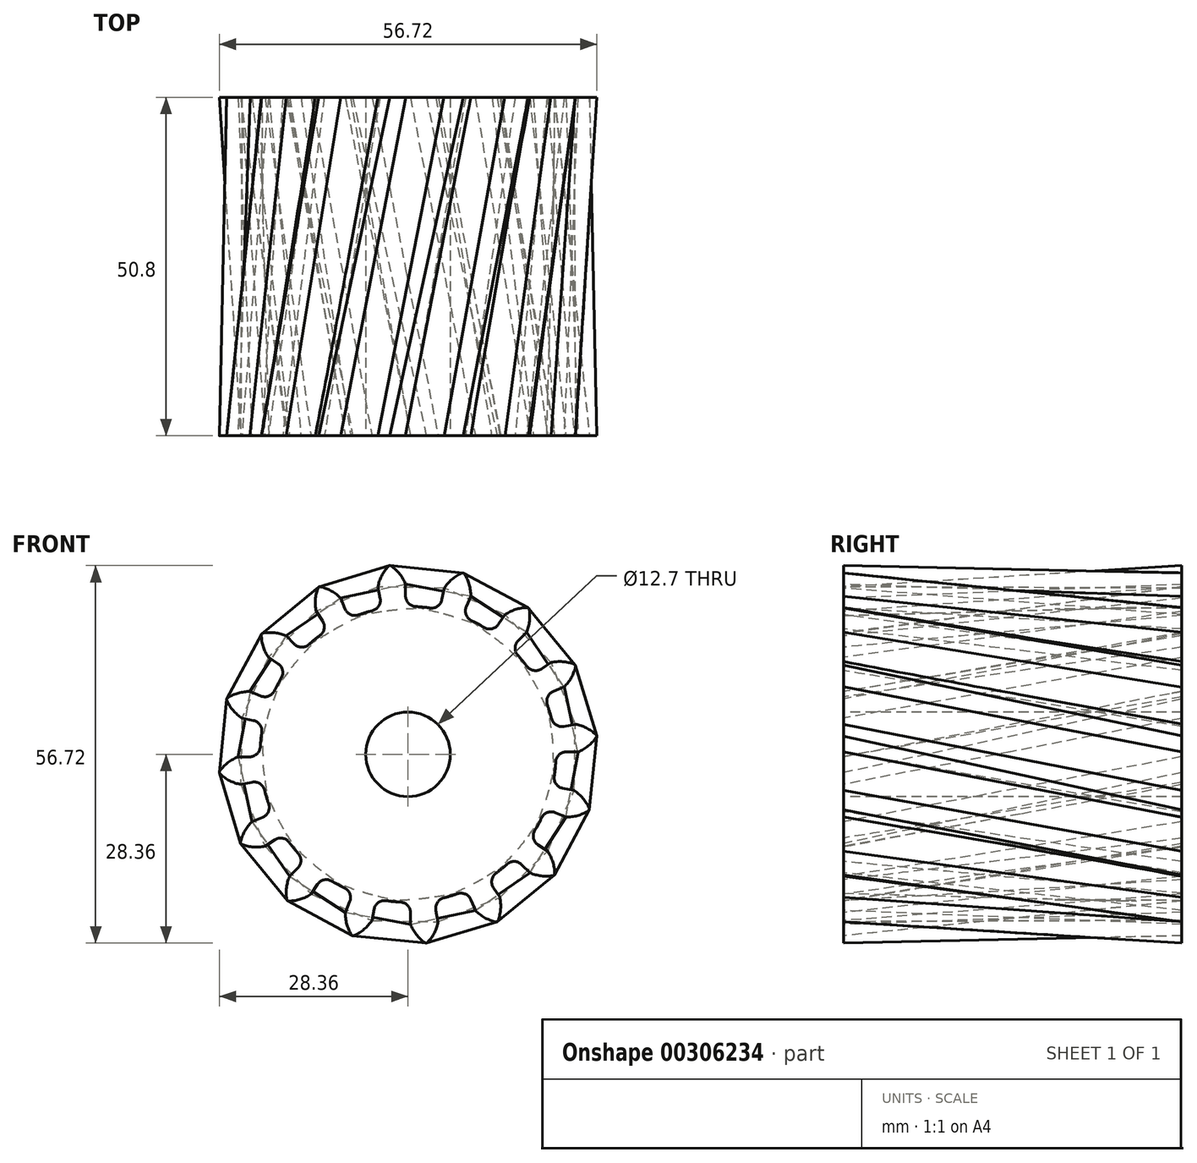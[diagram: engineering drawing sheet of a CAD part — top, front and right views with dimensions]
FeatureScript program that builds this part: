
annotation { "Feature Type Name" : "Feature", "Feature Type Description" : "" }
export const myFeature = defineFeature(function(context is Context, id is Id, definition is map)
    precondition{}
    {
        {
            var Q0;
            Q0=qCreatedBy(makeId("Front.planeOp"),FACE);
            var sketch = newSketch(context, id + "F0", { "sketchPlane" : qUnion([Q0])});
            skArc(sketch, "E0", {"start": v(-5.4, 21.56) * mm, "mid": v(-6.42, 21.28) * mm, "end": v(-7.42, 20.95) * mm});
            skLineSegment(sketch, "E1", {"start": v(0, 0) * mm, "end": v(-4.33, 44.68) * mm, "construction": true});
            skLineSegment(sketch, "E2", {"start": v(-2.75, 28.36) * mm, "end": v(-2.8, 28.36) * mm});
            skLineSegment(sketch, "E3", {"start": v(-0.36, 25.53) * mm, "end": v(-0.36, 23.8) * mm});
            skArc(sketch, "E4.trimOffspring", {"start": v(-0.36, 25.53) * mm, "mid": v(-1.24, 27.06) * mm, "end": v(-2.51, 28.27) * mm});
            skLineSegment(sketch, "E5.MirrorCS", {"start": v(-2.75, 28.36) * mm, "end": v(-2.7, 28.37) * mm});
            skArc(sketch, "E6.MirrorCS", {"start": v(-4.55, 25.13) * mm, "mid": v(-3.98, 26.8) * mm, "end": v(-2.97, 28.23) * mm});
            skLineSegment(sketch, "E7.MirrorCS", {"start": v(-4.55, 25.13) * mm, "end": v(-4.22, 23.42) * mm});
            skPoint(sketch, "E8.orphan", {"position": v(-3.74, 20.94) * mm});
            skPoint(sketch, "E9.orphan", {"position": v(-0.36, 21.27) * mm});
            skPoint(sketch, "E10.visualSharp", {"position": v(-3.92, 21.88) * mm});
            skArc(sketch, "E10.filletArc", {"start": v(-5.4, 21.56) * mm, "mid": v(-4.44, 22.25) * mm, "end": v(-4.22, 23.42) * mm});
            skPoint(sketch, "E11.visualSharp", {"position": v(-0.36, 22.22) * mm});
            skArc(sketch, "E11.filletArc", {"start": v(-0.36, 23.8) * mm, "mid": v(0.08, 22.7) * mm, "end": v(1.16, 22.2) * mm});
            skPoint(sketch, "E12.visualSharp", {"position": v(-2.65, 28.36) * mm});
            skArc(sketch, "E12.filletArc", {"start": v(-2.51, 28.27) * mm, "mid": v(-2.65, 28.34) * mm, "end": v(-2.8, 28.36) * mm});
            skPoint(sketch, "E13.visualSharp", {"position": v(-2.85, 28.34) * mm});
            skArc(sketch, "E13.filletArc", {"start": v(-2.7, 28.37) * mm, "mid": v(-2.84, 28.32) * mm, "end": v(-2.97, 28.23) * mm});
            skArc(sketch, "E14.1.0", {"start": v(-13.24, 17.85) * mm, "mid": v(-12.62, 18.86) * mm, "end": v(-12.86, 20.02) * mm});
            skLineSegment(sketch, "E14.1.1", {"start": v(-13.82, 21.47) * mm, "end": v(-12.86, 20.02) * mm});
            skArc(sketch, "E14.1.2", {"start": v(-13.82, 21.47) * mm, "mid": v(-13.93, 23.23) * mm, "end": v(-13.54, 24.94) * mm});
            skArc(sketch, "E14.1.3", {"start": v(-13.35, 25.18) * mm, "mid": v(-13.46, 25.08) * mm, "end": v(-13.54, 24.94) * mm});
            skLineSegment(sketch, "E14.1.4", {"start": v(-13.4, 25.15) * mm, "end": v(-13.35, 25.18) * mm});
            skLineSegment(sketch, "E14.1.5", {"start": v(-13.4, 25.15) * mm, "end": v(-13.45, 25.13) * mm});
            skArc(sketch, "E14.1.6", {"start": v(-13.14, 25.16) * mm, "mid": v(-13.3, 25.17) * mm, "end": v(-13.45, 25.13) * mm});
            skArc(sketch, "E14.1.7", {"start": v(-10.1, 23.45) * mm, "mid": v(-11.5, 24.52) * mm, "end": v(-13.14, 25.16) * mm});
            skLineSegment(sketch, "E14.1.8", {"start": v(-10.1, 23.45) * mm, "end": v(-9.43, 21.84) * mm});
            skArc(sketch, "E14.1.9", {"start": v(-9.43, 21.84) * mm, "mid": v(-8.6, 21) * mm, "end": v(-7.42, 20.95) * mm});
            skArc(sketch, "E14.2.0", {"start": v(-19.06, 11.42) * mm, "mid": v(-18.87, 12.6) * mm, "end": v(-19.54, 13.57) * mm});
            skLineSegment(sketch, "E14.2.1", {"start": v(-20.99, 14.55) * mm, "end": v(-19.54, 13.57) * mm});
            skArc(sketch, "E14.2.2", {"start": v(-20.99, 14.55) * mm, "mid": v(-21.76, 16.13) * mm, "end": v(-22.06, 17.86) * mm});
            skArc(sketch, "E14.2.3", {"start": v(-21.97, 18.16) * mm, "mid": v(-22.04, 18.02) * mm, "end": v(-22.06, 17.86) * mm});
            skLineSegment(sketch, "E14.2.4", {"start": v(-22, 18.11) * mm, "end": v(-21.97, 18.16) * mm});
            skLineSegment(sketch, "E14.2.5", {"start": v(-22, 18.11) * mm, "end": v(-22.04, 18.07) * mm});
            skArc(sketch, "E14.2.6", {"start": v(-21.77, 18.21) * mm, "mid": v(-21.91, 18.16) * mm, "end": v(-22.04, 18.07) * mm});
            skArc(sketch, "E14.2.7", {"start": v(-18.3, 17.8) * mm, "mid": v(-20, 18.26) * mm, "end": v(-21.77, 18.21) * mm});
            skLineSegment(sketch, "E14.2.8", {"start": v(-18.3, 17.8) * mm, "end": v(-17.08, 16.57) * mm});
            skArc(sketch, "E14.2.9", {"start": v(-17.08, 16.57) * mm, "mid": v(-15.99, 16.1) * mm, "end": v(-14.87, 16.51) * mm});
            skArc(sketch, "E14.3.0", {"start": v(-21.98, 3.26) * mm, "mid": v(-22.26, 4.41) * mm, "end": v(-23.25, 5.06) * mm});
            skLineSegment(sketch, "E14.3.1", {"start": v(-24.96, 5.4) * mm, "end": v(-23.25, 5.06) * mm});
            skArc(sketch, "E14.3.2", {"start": v(-24.96, 5.4) * mm, "mid": v(-26.28, 6.57) * mm, "end": v(-27.21, 8.06) * mm});
            skArc(sketch, "E14.3.3", {"start": v(-27.25, 8.37) * mm, "mid": v(-27.25, 8.21) * mm, "end": v(-27.21, 8.06) * mm});
            skLineSegment(sketch, "E14.3.4", {"start": v(-27.26, 8.31) * mm, "end": v(-27.25, 8.37) * mm});
            skLineSegment(sketch, "E14.3.5", {"start": v(-27.26, 8.31) * mm, "end": v(-27.28, 8.26) * mm});
            skArc(sketch, "E14.3.6", {"start": v(-27.08, 8.5) * mm, "mid": v(-27.2, 8.4) * mm, "end": v(-27.28, 8.26) * mm});
            skArc(sketch, "E14.3.7", {"start": v(-23.73, 9.44) * mm, "mid": v(-25.47, 9.21) * mm, "end": v(-27.08, 8.5) * mm});
            skLineSegment(sketch, "E14.3.8", {"start": v(-23.73, 9.44) * mm, "end": v(-22.12, 8.77) * mm});
            skArc(sketch, "E14.3.9", {"start": v(-22.12, 8.77) * mm, "mid": v(-20.93, 8.76) * mm, "end": v(-20.06, 9.56) * mm});
            skArc(sketch, "E14.4.0", {"start": v(-21.56, -5.4) * mm, "mid": v(-22.25, -4.44) * mm, "end": v(-23.42, -4.22) * mm});
            skLineSegment(sketch, "E14.4.1", {"start": v(-25.13, -4.55) * mm, "end": v(-23.42, -4.22) * mm});
            skArc(sketch, "E14.4.2", {"start": v(-25.13, -4.55) * mm, "mid": v(-26.8, -3.98) * mm, "end": v(-28.23, -2.97) * mm});
            skArc(sketch, "E14.4.3", {"start": v(-28.37, -2.7) * mm, "mid": v(-28.32, -2.84) * mm, "end": v(-28.23, -2.97) * mm});
            skLineSegment(sketch, "E14.4.4", {"start": v(-28.36, -2.75) * mm, "end": v(-28.37, -2.7) * mm});
            skLineSegment(sketch, "E14.4.5", {"start": v(-28.36, -2.75) * mm, "end": v(-28.36, -2.8) * mm});
            skArc(sketch, "E14.4.6", {"start": v(-28.27, -2.51) * mm, "mid": v(-28.34, -2.65) * mm, "end": v(-28.36, -2.8) * mm});
            skArc(sketch, "E14.4.7", {"start": v(-25.53, -0.36) * mm, "mid": v(-27.06, -1.24) * mm, "end": v(-28.27, -2.51) * mm});
            skLineSegment(sketch, "E14.4.8", {"start": v(-25.53, -0.36) * mm, "end": v(-23.8, -0.36) * mm});
            skArc(sketch, "E14.4.9", {"start": v(-23.8, -0.36) * mm, "mid": v(-22.7, 0.08) * mm, "end": v(-22.2, 1.16) * mm});
            skArc(sketch, "E14.5.0", {"start": v(-17.85, -13.24) * mm, "mid": v(-18.86, -12.62) * mm, "end": v(-20.02, -12.86) * mm});
            skLineSegment(sketch, "E14.5.1", {"start": v(-21.47, -13.82) * mm, "end": v(-20.02, -12.86) * mm});
            skArc(sketch, "E14.5.2", {"start": v(-21.47, -13.82) * mm, "mid": v(-23.23, -13.93) * mm, "end": v(-24.94, -13.54) * mm});
            skArc(sketch, "E14.5.3", {"start": v(-25.18, -13.35) * mm, "mid": v(-25.08, -13.46) * mm, "end": v(-24.94, -13.54) * mm});
            skLineSegment(sketch, "E14.5.4", {"start": v(-25.15, -13.4) * mm, "end": v(-25.18, -13.35) * mm});
            skLineSegment(sketch, "E14.5.5", {"start": v(-25.15, -13.4) * mm, "end": v(-25.13, -13.45) * mm});
            skArc(sketch, "E14.5.6", {"start": v(-25.16, -13.14) * mm, "mid": v(-25.17, -13.3) * mm, "end": v(-25.13, -13.45) * mm});
            skArc(sketch, "E14.5.7", {"start": v(-23.45, -10.1) * mm, "mid": v(-24.52, -11.5) * mm, "end": v(-25.16, -13.14) * mm});
            skLineSegment(sketch, "E14.5.8", {"start": v(-23.45, -10.1) * mm, "end": v(-21.84, -9.43) * mm});
            skArc(sketch, "E14.5.9", {"start": v(-21.84, -9.43) * mm, "mid": v(-21, -8.6) * mm, "end": v(-20.95, -7.42) * mm});
            skArc(sketch, "E14.6.0", {"start": v(-11.42, -19.06) * mm, "mid": v(-12.6, -18.87) * mm, "end": v(-13.57, -19.54) * mm});
            skLineSegment(sketch, "E14.6.1", {"start": v(-14.55, -20.99) * mm, "end": v(-13.57, -19.54) * mm});
            skArc(sketch, "E14.6.2", {"start": v(-14.55, -20.99) * mm, "mid": v(-16.13, -21.76) * mm, "end": v(-17.86, -22.06) * mm});
            skArc(sketch, "E14.6.3", {"start": v(-18.16, -21.97) * mm, "mid": v(-18.02, -22.04) * mm, "end": v(-17.86, -22.06) * mm});
            skLineSegment(sketch, "E14.6.4", {"start": v(-18.11, -22) * mm, "end": v(-18.16, -21.97) * mm});
            skLineSegment(sketch, "E14.6.5", {"start": v(-18.11, -22) * mm, "end": v(-18.07, -22.04) * mm});
            skArc(sketch, "E14.6.6", {"start": v(-18.21, -21.77) * mm, "mid": v(-18.16, -21.91) * mm, "end": v(-18.07, -22.04) * mm});
            skArc(sketch, "E14.6.7", {"start": v(-17.8, -18.3) * mm, "mid": v(-18.26, -20) * mm, "end": v(-18.21, -21.77) * mm});
            skLineSegment(sketch, "E14.6.8", {"start": v(-17.8, -18.3) * mm, "end": v(-16.57, -17.08) * mm});
            skArc(sketch, "E14.6.9", {"start": v(-16.57, -17.08) * mm, "mid": v(-16.1, -15.99) * mm, "end": v(-16.51, -14.87) * mm});
            skArc(sketch, "E14.7.0", {"start": v(-3.26, -21.98) * mm, "mid": v(-4.41, -22.26) * mm, "end": v(-5.06, -23.25) * mm});
            skLineSegment(sketch, "E14.7.1", {"start": v(-5.4, -24.96) * mm, "end": v(-5.06, -23.25) * mm});
            skArc(sketch, "E14.7.2", {"start": v(-5.4, -24.96) * mm, "mid": v(-6.57, -26.28) * mm, "end": v(-8.06, -27.21) * mm});
            skArc(sketch, "E14.7.3", {"start": v(-8.37, -27.25) * mm, "mid": v(-8.21, -27.25) * mm, "end": v(-8.06, -27.21) * mm});
            skLineSegment(sketch, "E14.7.4", {"start": v(-8.31, -27.26) * mm, "end": v(-8.37, -27.25) * mm});
            skLineSegment(sketch, "E14.7.5", {"start": v(-8.31, -27.26) * mm, "end": v(-8.26, -27.28) * mm});
            skArc(sketch, "E14.7.6", {"start": v(-8.5, -27.08) * mm, "mid": v(-8.4, -27.2) * mm, "end": v(-8.26, -27.28) * mm});
            skArc(sketch, "E14.7.7", {"start": v(-9.44, -23.73) * mm, "mid": v(-9.21, -25.47) * mm, "end": v(-8.5, -27.08) * mm});
            skLineSegment(sketch, "E14.7.8", {"start": v(-9.44, -23.73) * mm, "end": v(-8.77, -22.12) * mm});
            skArc(sketch, "E14.7.9", {"start": v(-8.77, -22.12) * mm, "mid": v(-8.76, -20.93) * mm, "end": v(-9.56, -20.06) * mm});
            skArc(sketch, "E14.8.0", {"start": v(5.4, -21.56) * mm, "mid": v(4.44, -22.25) * mm, "end": v(4.22, -23.42) * mm});
            skLineSegment(sketch, "E14.8.1", {"start": v(4.55, -25.13) * mm, "end": v(4.22, -23.42) * mm});
            skArc(sketch, "E14.8.2", {"start": v(4.55, -25.13) * mm, "mid": v(3.98, -26.8) * mm, "end": v(2.97, -28.23) * mm});
            skArc(sketch, "E14.8.3", {"start": v(2.7, -28.37) * mm, "mid": v(2.84, -28.32) * mm, "end": v(2.97, -28.23) * mm});
            skLineSegment(sketch, "E14.8.4", {"start": v(2.75, -28.36) * mm, "end": v(2.7, -28.37) * mm});
            skLineSegment(sketch, "E14.8.5", {"start": v(2.75, -28.36) * mm, "end": v(2.8, -28.36) * mm});
            skArc(sketch, "E14.8.6", {"start": v(2.51, -28.27) * mm, "mid": v(2.65, -28.34) * mm, "end": v(2.8, -28.36) * mm});
            skArc(sketch, "E14.8.7", {"start": v(0.36, -25.53) * mm, "mid": v(1.24, -27.06) * mm, "end": v(2.51, -28.27) * mm});
            skLineSegment(sketch, "E14.8.8", {"start": v(0.36, -25.53) * mm, "end": v(0.36, -23.8) * mm});
            skArc(sketch, "E14.8.9", {"start": v(0.36, -23.8) * mm, "mid": v(-0.08, -22.7) * mm, "end": v(-1.16, -22.2) * mm});
            skArc(sketch, "E14.9.0", {"start": v(13.24, -17.85) * mm, "mid": v(12.62, -18.86) * mm, "end": v(12.86, -20.02) * mm});
            skLineSegment(sketch, "E14.9.1", {"start": v(13.82, -21.47) * mm, "end": v(12.86, -20.02) * mm});
            skArc(sketch, "E14.9.2", {"start": v(13.82, -21.47) * mm, "mid": v(13.93, -23.23) * mm, "end": v(13.54, -24.94) * mm});
            skArc(sketch, "E14.9.3", {"start": v(13.35, -25.18) * mm, "mid": v(13.46, -25.08) * mm, "end": v(13.54, -24.94) * mm});
            skLineSegment(sketch, "E14.9.4", {"start": v(13.4, -25.15) * mm, "end": v(13.35, -25.18) * mm});
            skLineSegment(sketch, "E14.9.5", {"start": v(13.4, -25.15) * mm, "end": v(13.45, -25.13) * mm});
            skArc(sketch, "E14.9.6", {"start": v(13.14, -25.16) * mm, "mid": v(13.3, -25.17) * mm, "end": v(13.45, -25.13) * mm});
            skArc(sketch, "E14.9.7", {"start": v(10.1, -23.45) * mm, "mid": v(11.5, -24.52) * mm, "end": v(13.14, -25.16) * mm});
            skLineSegment(sketch, "E14.9.8", {"start": v(10.1, -23.45) * mm, "end": v(9.43, -21.84) * mm});
            skArc(sketch, "E14.9.9", {"start": v(9.43, -21.84) * mm, "mid": v(8.6, -21) * mm, "end": v(7.42, -20.95) * mm});
            skArc(sketch, "E14.10.0", {"start": v(19.06, -11.42) * mm, "mid": v(18.87, -12.6) * mm, "end": v(19.54, -13.57) * mm});
            skLineSegment(sketch, "E14.10.1", {"start": v(20.99, -14.55) * mm, "end": v(19.54, -13.57) * mm});
            skArc(sketch, "E14.10.2", {"start": v(20.99, -14.55) * mm, "mid": v(21.76, -16.13) * mm, "end": v(22.06, -17.86) * mm});
            skArc(sketch, "E14.10.3", {"start": v(21.97, -18.16) * mm, "mid": v(22.04, -18.02) * mm, "end": v(22.06, -17.86) * mm});
            skLineSegment(sketch, "E14.10.4", {"start": v(22, -18.11) * mm, "end": v(21.97, -18.16) * mm});
            skLineSegment(sketch, "E14.10.5", {"start": v(22, -18.11) * mm, "end": v(22.04, -18.07) * mm});
            skArc(sketch, "E14.10.6", {"start": v(21.77, -18.21) * mm, "mid": v(21.91, -18.16) * mm, "end": v(22.04, -18.07) * mm});
            skArc(sketch, "E14.10.7", {"start": v(18.3, -17.8) * mm, "mid": v(20, -18.26) * mm, "end": v(21.77, -18.21) * mm});
            skLineSegment(sketch, "E14.10.8", {"start": v(18.3, -17.8) * mm, "end": v(17.08, -16.57) * mm});
            skArc(sketch, "E14.10.9", {"start": v(17.08, -16.57) * mm, "mid": v(15.99, -16.1) * mm, "end": v(14.87, -16.51) * mm});
            skArc(sketch, "E14.11.0", {"start": v(21.98, -3.26) * mm, "mid": v(22.26, -4.41) * mm, "end": v(23.25, -5.06) * mm});
            skLineSegment(sketch, "E14.11.1", {"start": v(24.96, -5.4) * mm, "end": v(23.25, -5.06) * mm});
            skArc(sketch, "E14.11.2", {"start": v(24.96, -5.4) * mm, "mid": v(26.28, -6.57) * mm, "end": v(27.21, -8.06) * mm});
            skArc(sketch, "E14.11.3", {"start": v(27.25, -8.37) * mm, "mid": v(27.25, -8.21) * mm, "end": v(27.21, -8.06) * mm});
            skLineSegment(sketch, "E14.11.4", {"start": v(27.26, -8.31) * mm, "end": v(27.25, -8.37) * mm});
            skLineSegment(sketch, "E14.11.5", {"start": v(27.26, -8.31) * mm, "end": v(27.28, -8.26) * mm});
            skArc(sketch, "E14.11.6", {"start": v(27.08, -8.5) * mm, "mid": v(27.2, -8.4) * mm, "end": v(27.28, -8.26) * mm});
            skArc(sketch, "E14.11.7", {"start": v(23.73, -9.44) * mm, "mid": v(25.47, -9.21) * mm, "end": v(27.08, -8.5) * mm});
            skLineSegment(sketch, "E14.11.8", {"start": v(23.73, -9.44) * mm, "end": v(22.12, -8.77) * mm});
            skArc(sketch, "E14.11.9", {"start": v(22.12, -8.77) * mm, "mid": v(20.93, -8.76) * mm, "end": v(20.06, -9.56) * mm});
            skArc(sketch, "E14.12.0", {"start": v(21.56, 5.4) * mm, "mid": v(22.25, 4.44) * mm, "end": v(23.42, 4.22) * mm});
            skLineSegment(sketch, "E14.12.1", {"start": v(25.13, 4.55) * mm, "end": v(23.42, 4.22) * mm});
            skArc(sketch, "E14.12.2", {"start": v(25.13, 4.55) * mm, "mid": v(26.8, 3.98) * mm, "end": v(28.23, 2.97) * mm});
            skArc(sketch, "E14.12.3", {"start": v(28.37, 2.7) * mm, "mid": v(28.32, 2.84) * mm, "end": v(28.23, 2.97) * mm});
            skLineSegment(sketch, "E14.12.4", {"start": v(28.36, 2.75) * mm, "end": v(28.37, 2.7) * mm});
            skLineSegment(sketch, "E14.12.5", {"start": v(28.36, 2.75) * mm, "end": v(28.36, 2.8) * mm});
            skArc(sketch, "E14.12.6", {"start": v(28.27, 2.51) * mm, "mid": v(28.34, 2.65) * mm, "end": v(28.36, 2.8) * mm});
            skArc(sketch, "E14.12.7", {"start": v(25.53, 0.36) * mm, "mid": v(27.06, 1.24) * mm, "end": v(28.27, 2.51) * mm});
            skLineSegment(sketch, "E14.12.8", {"start": v(25.53, 0.36) * mm, "end": v(23.8, 0.36) * mm});
            skArc(sketch, "E14.12.9", {"start": v(23.8, 0.36) * mm, "mid": v(22.7, -0.08) * mm, "end": v(22.2, -1.16) * mm});
            skArc(sketch, "E14.13.0", {"start": v(17.85, 13.24) * mm, "mid": v(18.86, 12.62) * mm, "end": v(20.02, 12.86) * mm});
            skLineSegment(sketch, "E14.13.1", {"start": v(21.47, 13.82) * mm, "end": v(20.02, 12.86) * mm});
            skArc(sketch, "E14.13.2", {"start": v(21.47, 13.82) * mm, "mid": v(23.23, 13.93) * mm, "end": v(24.94, 13.54) * mm});
            skArc(sketch, "E14.13.3", {"start": v(25.18, 13.35) * mm, "mid": v(25.08, 13.46) * mm, "end": v(24.94, 13.54) * mm});
            skLineSegment(sketch, "E14.13.4", {"start": v(25.15, 13.4) * mm, "end": v(25.18, 13.35) * mm});
            skLineSegment(sketch, "E14.13.5", {"start": v(25.15, 13.4) * mm, "end": v(25.13, 13.45) * mm});
            skArc(sketch, "E14.13.6", {"start": v(25.16, 13.14) * mm, "mid": v(25.17, 13.3) * mm, "end": v(25.13, 13.45) * mm});
            skArc(sketch, "E14.13.7", {"start": v(23.45, 10.1) * mm, "mid": v(24.52, 11.5) * mm, "end": v(25.16, 13.14) * mm});
            skLineSegment(sketch, "E14.13.8", {"start": v(23.45, 10.1) * mm, "end": v(21.84, 9.43) * mm});
            skArc(sketch, "E14.13.9", {"start": v(21.84, 9.43) * mm, "mid": v(21, 8.6) * mm, "end": v(20.95, 7.42) * mm});
            skArc(sketch, "E14.14.0", {"start": v(11.42, 19.06) * mm, "mid": v(12.6, 18.87) * mm, "end": v(13.57, 19.54) * mm});
            skLineSegment(sketch, "E14.14.1", {"start": v(14.55, 20.99) * mm, "end": v(13.57, 19.54) * mm});
            skArc(sketch, "E14.14.2", {"start": v(14.55, 20.99) * mm, "mid": v(16.13, 21.76) * mm, "end": v(17.86, 22.06) * mm});
            skArc(sketch, "E14.14.3", {"start": v(18.16, 21.97) * mm, "mid": v(18.02, 22.04) * mm, "end": v(17.86, 22.06) * mm});
            skLineSegment(sketch, "E14.14.4", {"start": v(18.11, 22) * mm, "end": v(18.16, 21.97) * mm});
            skLineSegment(sketch, "E14.14.5", {"start": v(18.11, 22) * mm, "end": v(18.07, 22.04) * mm});
            skArc(sketch, "E14.14.6", {"start": v(18.21, 21.77) * mm, "mid": v(18.16, 21.91) * mm, "end": v(18.07, 22.04) * mm});
            skArc(sketch, "E14.14.7", {"start": v(17.8, 18.3) * mm, "mid": v(18.26, 20) * mm, "end": v(18.21, 21.77) * mm});
            skLineSegment(sketch, "E14.14.8", {"start": v(17.8, 18.3) * mm, "end": v(16.57, 17.08) * mm});
            skArc(sketch, "E14.14.9", {"start": v(16.57, 17.08) * mm, "mid": v(16.1, 15.99) * mm, "end": v(16.51, 14.87) * mm});
            skArc(sketch, "E14.15.0", {"start": v(3.26, 21.98) * mm, "mid": v(4.41, 22.26) * mm, "end": v(5.06, 23.25) * mm});
            skLineSegment(sketch, "E14.15.1", {"start": v(5.4, 24.96) * mm, "end": v(5.06, 23.25) * mm});
            skArc(sketch, "E14.15.2", {"start": v(5.4, 24.96) * mm, "mid": v(6.57, 26.28) * mm, "end": v(8.06, 27.21) * mm});
            skArc(sketch, "E14.15.3", {"start": v(8.37, 27.25) * mm, "mid": v(8.21, 27.25) * mm, "end": v(8.06, 27.21) * mm});
            skLineSegment(sketch, "E14.15.4", {"start": v(8.31, 27.26) * mm, "end": v(8.37, 27.25) * mm});
            skLineSegment(sketch, "E14.15.5", {"start": v(8.31, 27.26) * mm, "end": v(8.26, 27.28) * mm});
            skArc(sketch, "E14.15.6", {"start": v(8.5, 27.08) * mm, "mid": v(8.4, 27.2) * mm, "end": v(8.26, 27.28) * mm});
            skArc(sketch, "E14.15.7", {"start": v(9.44, 23.73) * mm, "mid": v(9.21, 25.47) * mm, "end": v(8.5, 27.08) * mm});
            skLineSegment(sketch, "E14.15.8", {"start": v(9.44, 23.73) * mm, "end": v(8.77, 22.12) * mm});
            skArc(sketch, "E14.15.9", {"start": v(8.77, 22.12) * mm, "mid": v(8.76, 20.93) * mm, "end": v(9.56, 20.06) * mm});
            skArc(sketch, "E15.trimOffspring", {"start": v(-13.24, 17.85) * mm, "mid": v(-14.07, 17.2) * mm, "end": v(-14.87, 16.51) * mm});
            skArc(sketch, "E16.trimOffspring", {"start": v(-19.06, 11.42) * mm, "mid": v(-19.58, 10.5) * mm, "end": v(-20.06, 9.56) * mm});
            skArc(sketch, "E17.trimOffspring", {"start": v(-21.98, 3.26) * mm, "mid": v(-22.11, 2.21) * mm, "end": v(-22.2, 1.16) * mm});
            skArc(sketch, "E18.trimOffspring", {"start": v(-21.56, -5.4) * mm, "mid": v(-21.28, -6.42) * mm, "end": v(-20.95, -7.42) * mm});
            skArc(sketch, "E19.trimOffspring", {"start": v(-17.85, -13.24) * mm, "mid": v(-17.2, -14.07) * mm, "end": v(-16.51, -14.87) * mm});
            skArc(sketch, "E20.trimOffspring", {"start": v(-11.42, -19.06) * mm, "mid": v(-10.5, -19.58) * mm, "end": v(-9.56, -20.06) * mm});
            skArc(sketch, "E21.trimOffspring", {"start": v(-3.26, -21.98) * mm, "mid": v(-2.21, -22.11) * mm, "end": v(-1.16, -22.2) * mm});
            skArc(sketch, "E22.trimOffspring", {"start": v(5.4, -21.56) * mm, "mid": v(6.42, -21.28) * mm, "end": v(7.42, -20.95) * mm});
            skArc(sketch, "E23.trimOffspring", {"start": v(13.24, -17.85) * mm, "mid": v(14.07, -17.2) * mm, "end": v(14.87, -16.51) * mm});
            skArc(sketch, "E24.trimOffspring", {"start": v(19.06, -11.42) * mm, "mid": v(19.58, -10.5) * mm, "end": v(20.06, -9.56) * mm});
            skArc(sketch, "E25.trimOffspring", {"start": v(21.98, -3.26) * mm, "mid": v(22.11, -2.21) * mm, "end": v(22.2, -1.16) * mm});
            skArc(sketch, "E26.trimOffspring", {"start": v(21.56, 5.4) * mm, "mid": v(21.28, 6.42) * mm, "end": v(20.95, 7.42) * mm});
            skArc(sketch, "E27.trimOffspring", {"start": v(17.85, 13.24) * mm, "mid": v(17.2, 14.07) * mm, "end": v(16.51, 14.87) * mm});
            skArc(sketch, "E28.trimOffspring", {"start": v(11.42, 19.06) * mm, "mid": v(10.5, 19.58) * mm, "end": v(9.56, 20.06) * mm});
            skArc(sketch, "E29.trimOffspring", {"start": v(3.26, 21.98) * mm, "mid": v(2.21, 22.11) * mm, "end": v(1.16, 22.2) * mm});
            skSolve(sketch);
        }
        {
            var Q0;
            Q0=makeQuery(id+"F0.imprint","IMPRINT",FACE,{"disambiguationData":[TD([[makeQuery(id+"F0.imprint","IMPRINT",EDGE,{"derivedFrom":sQuery(id+"F0.wireOp",EDGE,"E0")}),1.0]])]});
            cPlane(context, id + "F1", {"entities" : qUnion([Q0]), "cplaneType" : CPlaneType.OFFSET, "offset" : 50.8 * mm, "width" : 152.4 * mm, "height" : 152.4 * mm});
        }
        {
            var Q0;
            Q0=qCreatedBy(id+"F1.planeOp",FACE);
            var sketch = newSketch(context, id + "F2", { "sketchPlane" : qUnion([Q0])});
            skArc(sketch, "E30", {"start": v(-5.37, 21.57) * mm, "mid": v(-6.41, 21.28) * mm, "end": v(-7.44, 20.94) * mm});
            skLineSegment(sketch, "E31", {"start": v(0, 0) * mm, "end": v(-3.83, 39.63) * mm, "construction": true});
            skLineSegment(sketch, "E32", {"start": v(-2.74, 28.35) * mm, "end": v(-2.8, 28.35) * mm});
            skLineSegment(sketch, "E33", {"start": v(-0.37, 25.55) * mm, "end": v(-0.38, 23.8) * mm});
            skArc(sketch, "E34.trimOffspring", {"start": v(-0.37, 25.55) * mm, "mid": v(-1.24, 27.05) * mm, "end": v(-2.5, 28.26) * mm});
            skLineSegment(sketch, "E35.MirrorCS", {"start": v(-2.74, 28.35) * mm, "end": v(-2.7, 28.36) * mm});
            skArc(sketch, "E36.MirrorCS", {"start": v(-4.53, 25.15) * mm, "mid": v(-3.96, 26.8) * mm, "end": v(-2.96, 28.21) * mm});
            skLineSegment(sketch, "E37.MirrorCS", {"start": v(-4.53, 25.15) * mm, "end": v(-4.19, 23.43) * mm});
            skPoint(sketch, "E38.visualSharp", {"position": v(-2.85, 28.33) * mm});
            skArc(sketch, "E38.filletArc", {"start": v(-2.7, 28.36) * mm, "mid": v(-2.84, 28.31) * mm, "end": v(-2.96, 28.21) * mm});
            skPoint(sketch, "E39.visualSharp", {"position": v(-2.63, 28.35) * mm});
            skArc(sketch, "E39.filletArc", {"start": v(-2.5, 28.26) * mm, "mid": v(-2.64, 28.33) * mm, "end": v(-2.8, 28.35) * mm});
            skPoint(sketch, "E40.orphan", {"position": v(-3.7, 20.97) * mm});
            skPoint(sketch, "E41.orphan", {"position": v(-0.38, 21.3) * mm});
            skPoint(sketch, "E42.visualSharp", {"position": v(-3.89, 21.88) * mm});
            skArc(sketch, "E42.filletArc", {"start": v(-5.37, 21.57) * mm, "mid": v(-4.4, 22.26) * mm, "end": v(-4.19, 23.43) * mm});
            skPoint(sketch, "E43.visualSharp", {"position": v(-0.38, 22.22) * mm});
            skArc(sketch, "E43.filletArc", {"start": v(-0.38, 23.8) * mm, "mid": v(0.06, 22.7) * mm, "end": v(1.14, 22.2) * mm});
            skArc(sketch, "E44.1.0", {"start": v(-13.22, 17.87) * mm, "mid": v(-12.6, 18.88) * mm, "end": v(-12.83, 20.04) * mm});
            skLineSegment(sketch, "E44.1.1", {"start": v(-13.8, 21.5) * mm, "end": v(-12.83, 20.04) * mm});
            skArc(sketch, "E44.1.2", {"start": v(-13.8, 21.5) * mm, "mid": v(-13.92, 23.23) * mm, "end": v(-13.54, 24.93) * mm});
            skArc(sketch, "E44.1.3", {"start": v(-13.34, 25.17) * mm, "mid": v(-13.46, 25.07) * mm, "end": v(-13.54, 24.93) * mm});
            skLineSegment(sketch, "E44.1.4", {"start": v(-13.38, 25.15) * mm, "end": v(-13.34, 25.17) * mm});
            skLineSegment(sketch, "E44.1.5", {"start": v(-13.38, 25.15) * mm, "end": v(-13.43, 25.13) * mm});
            skArc(sketch, "E44.1.6", {"start": v(-13.12, 25.15) * mm, "mid": v(-13.28, 25.16) * mm, "end": v(-13.43, 25.13) * mm});
            skArc(sketch, "E44.1.7", {"start": v(-10.12, 23.46) * mm, "mid": v(-11.5, 24.52) * mm, "end": v(-13.12, 25.15) * mm});
            skLineSegment(sketch, "E44.1.8", {"start": v(-10.12, 23.46) * mm, "end": v(-9.45, 21.84) * mm});
            skArc(sketch, "E44.1.9", {"start": v(-9.45, 21.84) * mm, "mid": v(-8.62, 20.99) * mm, "end": v(-7.44, 20.94) * mm});
            skArc(sketch, "E44.2.0", {"start": v(-19.05, 11.45) * mm, "mid": v(-18.86, 12.62) * mm, "end": v(-19.53, 13.6) * mm});
            skLineSegment(sketch, "E44.2.1", {"start": v(-20.98, 14.58) * mm, "end": v(-19.53, 13.6) * mm});
            skArc(sketch, "E44.2.2", {"start": v(-20.98, 14.58) * mm, "mid": v(-21.75, 16.14) * mm, "end": v(-22.05, 17.85) * mm});
            skArc(sketch, "E44.2.3", {"start": v(-21.96, 18.15) * mm, "mid": v(-22.03, 18.01) * mm, "end": v(-22.05, 17.85) * mm});
            skLineSegment(sketch, "E44.2.4", {"start": v(-21.99, 18.11) * mm, "end": v(-21.96, 18.15) * mm});
            skLineSegment(sketch, "E44.2.5", {"start": v(-21.99, 18.11) * mm, "end": v(-22.02, 18.08) * mm});
            skArc(sketch, "E44.2.6", {"start": v(-21.75, 18.22) * mm, "mid": v(-21.9, 18.17) * mm, "end": v(-22.02, 18.08) * mm});
            skArc(sketch, "E44.2.7", {"start": v(-18.33, 17.8) * mm, "mid": v(-20, 18.25) * mm, "end": v(-21.75, 18.22) * mm});
            skLineSegment(sketch, "E44.2.8", {"start": v(-18.33, 17.8) * mm, "end": v(-17.1, 16.56) * mm});
            skArc(sketch, "E44.2.9", {"start": v(-17.1, 16.56) * mm, "mid": v(-16, 16.1) * mm, "end": v(-14.89, 16.5) * mm});
            skArc(sketch, "E44.3.0", {"start": v(-21.98, 3.29) * mm, "mid": v(-22.25, 4.44) * mm, "end": v(-23.25, 5.1) * mm});
            skLineSegment(sketch, "E44.3.1", {"start": v(-24.96, 5.44) * mm, "end": v(-23.25, 5.1) * mm});
            skArc(sketch, "E44.3.2", {"start": v(-24.96, 5.44) * mm, "mid": v(-26.27, 6.59) * mm, "end": v(-27.2, 8.06) * mm});
            skArc(sketch, "E44.3.3", {"start": v(-27.23, 8.37) * mm, "mid": v(-27.24, 8.21) * mm, "end": v(-27.2, 8.06) * mm});
            skLineSegment(sketch, "E44.3.4", {"start": v(-27.24, 8.32) * mm, "end": v(-27.23, 8.37) * mm});
            skLineSegment(sketch, "E44.3.5", {"start": v(-27.24, 8.32) * mm, "end": v(-27.26, 8.27) * mm});
            skArc(sketch, "E44.3.6", {"start": v(-27.06, 8.5) * mm, "mid": v(-27.18, 8.4) * mm, "end": v(-27.26, 8.27) * mm});
            skArc(sketch, "E44.3.7", {"start": v(-23.74, 9.43) * mm, "mid": v(-25.47, 9.2) * mm, "end": v(-27.06, 8.5) * mm});
            skLineSegment(sketch, "E44.3.8", {"start": v(-23.74, 9.43) * mm, "end": v(-22.13, 8.76) * mm});
            skArc(sketch, "E44.3.9", {"start": v(-22.13, 8.76) * mm, "mid": v(-20.94, 8.74) * mm, "end": v(-20.07, 9.55) * mm});
            skArc(sketch, "E44.4.0", {"start": v(-21.57, -5.37) * mm, "mid": v(-22.26, -4.4) * mm, "end": v(-23.43, -4.19) * mm});
            skLineSegment(sketch, "E44.4.1", {"start": v(-25.15, -4.53) * mm, "end": v(-23.43, -4.19) * mm});
            skArc(sketch, "E44.4.2", {"start": v(-25.15, -4.53) * mm, "mid": v(-26.8, -3.96) * mm, "end": v(-28.21, -2.96) * mm});
            skArc(sketch, "E44.4.3", {"start": v(-28.36, -2.7) * mm, "mid": v(-28.31, -2.84) * mm, "end": v(-28.21, -2.96) * mm});
            skLineSegment(sketch, "E44.4.4", {"start": v(-28.35, -2.74) * mm, "end": v(-28.36, -2.7) * mm});
            skLineSegment(sketch, "E44.4.5", {"start": v(-28.35, -2.74) * mm, "end": v(-28.35, -2.8) * mm});
            skArc(sketch, "E44.4.6", {"start": v(-28.26, -2.5) * mm, "mid": v(-28.33, -2.64) * mm, "end": v(-28.35, -2.8) * mm});
            skArc(sketch, "E44.4.7", {"start": v(-25.55, -0.37) * mm, "mid": v(-27.05, -1.24) * mm, "end": v(-28.26, -2.5) * mm});
            skLineSegment(sketch, "E44.4.8", {"start": v(-25.55, -0.37) * mm, "end": v(-23.8, -0.38) * mm});
            skArc(sketch, "E44.4.9", {"start": v(-23.8, -0.38) * mm, "mid": v(-22.7, 0.06) * mm, "end": v(-22.2, 1.14) * mm});
            skArc(sketch, "E44.5.0", {"start": v(-17.87, -13.22) * mm, "mid": v(-18.88, -12.6) * mm, "end": v(-20.04, -12.83) * mm});
            skLineSegment(sketch, "E44.5.1", {"start": v(-21.5, -13.8) * mm, "end": v(-20.04, -12.83) * mm});
            skArc(sketch, "E44.5.2", {"start": v(-21.5, -13.8) * mm, "mid": v(-23.23, -13.92) * mm, "end": v(-24.93, -13.54) * mm});
            skArc(sketch, "E44.5.3", {"start": v(-25.17, -13.34) * mm, "mid": v(-25.07, -13.46) * mm, "end": v(-24.93, -13.54) * mm});
            skLineSegment(sketch, "E44.5.4", {"start": v(-25.15, -13.38) * mm, "end": v(-25.17, -13.34) * mm});
            skLineSegment(sketch, "E44.5.5", {"start": v(-25.15, -13.38) * mm, "end": v(-25.13, -13.43) * mm});
            skArc(sketch, "E44.5.6", {"start": v(-25.15, -13.12) * mm, "mid": v(-25.16, -13.28) * mm, "end": v(-25.13, -13.43) * mm});
            skArc(sketch, "E44.5.7", {"start": v(-23.46, -10.12) * mm, "mid": v(-24.52, -11.5) * mm, "end": v(-25.15, -13.12) * mm});
            skLineSegment(sketch, "E44.5.8", {"start": v(-23.46, -10.12) * mm, "end": v(-21.84, -9.45) * mm});
            skArc(sketch, "E44.5.9", {"start": v(-21.84, -9.45) * mm, "mid": v(-20.99, -8.62) * mm, "end": v(-20.94, -7.44) * mm});
            skArc(sketch, "E44.6.0", {"start": v(-11.45, -19.05) * mm, "mid": v(-12.62, -18.86) * mm, "end": v(-13.6, -19.53) * mm});
            skLineSegment(sketch, "E44.6.1", {"start": v(-14.58, -20.98) * mm, "end": v(-13.6, -19.53) * mm});
            skArc(sketch, "E44.6.2", {"start": v(-14.58, -20.98) * mm, "mid": v(-16.14, -21.75) * mm, "end": v(-17.85, -22.05) * mm});
            skArc(sketch, "E44.6.3", {"start": v(-18.15, -21.96) * mm, "mid": v(-18.01, -22.03) * mm, "end": v(-17.85, -22.05) * mm});
            skLineSegment(sketch, "E44.6.4", {"start": v(-18.11, -21.99) * mm, "end": v(-18.15, -21.96) * mm});
            skLineSegment(sketch, "E44.6.5", {"start": v(-18.11, -21.99) * mm, "end": v(-18.08, -22.02) * mm});
            skArc(sketch, "E44.6.6", {"start": v(-18.22, -21.75) * mm, "mid": v(-18.17, -21.9) * mm, "end": v(-18.08, -22.02) * mm});
            skArc(sketch, "E44.6.7", {"start": v(-17.8, -18.33) * mm, "mid": v(-18.25, -20) * mm, "end": v(-18.22, -21.75) * mm});
            skLineSegment(sketch, "E44.6.8", {"start": v(-17.8, -18.33) * mm, "end": v(-16.56, -17.1) * mm});
            skArc(sketch, "E44.6.9", {"start": v(-16.56, -17.1) * mm, "mid": v(-16.1, -16) * mm, "end": v(-16.5, -14.89) * mm});
            skArc(sketch, "E44.7.0", {"start": v(-3.29, -21.98) * mm, "mid": v(-4.44, -22.25) * mm, "end": v(-5.1, -23.25) * mm});
            skLineSegment(sketch, "E44.7.1", {"start": v(-5.44, -24.96) * mm, "end": v(-5.1, -23.25) * mm});
            skArc(sketch, "E44.7.2", {"start": v(-5.44, -24.96) * mm, "mid": v(-6.59, -26.27) * mm, "end": v(-8.06, -27.2) * mm});
            skArc(sketch, "E44.7.3", {"start": v(-8.37, -27.23) * mm, "mid": v(-8.21, -27.24) * mm, "end": v(-8.06, -27.2) * mm});
            skLineSegment(sketch, "E44.7.4", {"start": v(-8.32, -27.24) * mm, "end": v(-8.37, -27.23) * mm});
            skLineSegment(sketch, "E44.7.5", {"start": v(-8.32, -27.24) * mm, "end": v(-8.27, -27.26) * mm});
            skArc(sketch, "E44.7.6", {"start": v(-8.5, -27.06) * mm, "mid": v(-8.4, -27.18) * mm, "end": v(-8.27, -27.26) * mm});
            skArc(sketch, "E44.7.7", {"start": v(-9.43, -23.74) * mm, "mid": v(-9.2, -25.47) * mm, "end": v(-8.5, -27.06) * mm});
            skLineSegment(sketch, "E44.7.8", {"start": v(-9.43, -23.74) * mm, "end": v(-8.76, -22.13) * mm});
            skArc(sketch, "E44.7.9", {"start": v(-8.76, -22.13) * mm, "mid": v(-8.74, -20.94) * mm, "end": v(-9.55, -20.07) * mm});
            skArc(sketch, "E44.8.0", {"start": v(5.37, -21.57) * mm, "mid": v(4.4, -22.26) * mm, "end": v(4.19, -23.43) * mm});
            skLineSegment(sketch, "E44.8.1", {"start": v(4.53, -25.15) * mm, "end": v(4.19, -23.43) * mm});
            skArc(sketch, "E44.8.2", {"start": v(4.53, -25.15) * mm, "mid": v(3.96, -26.8) * mm, "end": v(2.96, -28.21) * mm});
            skArc(sketch, "E44.8.3", {"start": v(2.7, -28.36) * mm, "mid": v(2.84, -28.31) * mm, "end": v(2.96, -28.21) * mm});
            skLineSegment(sketch, "E44.8.4", {"start": v(2.74, -28.35) * mm, "end": v(2.7, -28.36) * mm});
            skLineSegment(sketch, "E44.8.5", {"start": v(2.74, -28.35) * mm, "end": v(2.8, -28.35) * mm});
            skArc(sketch, "E44.8.6", {"start": v(2.5, -28.26) * mm, "mid": v(2.64, -28.33) * mm, "end": v(2.8, -28.35) * mm});
            skArc(sketch, "E44.8.7", {"start": v(0.37, -25.55) * mm, "mid": v(1.24, -27.05) * mm, "end": v(2.5, -28.26) * mm});
            skLineSegment(sketch, "E44.8.8", {"start": v(0.37, -25.55) * mm, "end": v(0.38, -23.8) * mm});
            skArc(sketch, "E44.8.9", {"start": v(0.38, -23.8) * mm, "mid": v(-0.06, -22.7) * mm, "end": v(-1.14, -22.2) * mm});
            skArc(sketch, "E44.9.0", {"start": v(13.22, -17.87) * mm, "mid": v(12.6, -18.88) * mm, "end": v(12.83, -20.04) * mm});
            skLineSegment(sketch, "E44.9.1", {"start": v(13.8, -21.5) * mm, "end": v(12.83, -20.04) * mm});
            skArc(sketch, "E44.9.2", {"start": v(13.8, -21.5) * mm, "mid": v(13.92, -23.23) * mm, "end": v(13.54, -24.93) * mm});
            skArc(sketch, "E44.9.3", {"start": v(13.34, -25.17) * mm, "mid": v(13.46, -25.07) * mm, "end": v(13.54, -24.93) * mm});
            skLineSegment(sketch, "E44.9.4", {"start": v(13.38, -25.15) * mm, "end": v(13.34, -25.17) * mm});
            skLineSegment(sketch, "E44.9.5", {"start": v(13.38, -25.15) * mm, "end": v(13.43, -25.13) * mm});
            skArc(sketch, "E44.9.6", {"start": v(13.12, -25.15) * mm, "mid": v(13.28, -25.16) * mm, "end": v(13.43, -25.13) * mm});
            skArc(sketch, "E44.9.7", {"start": v(10.12, -23.46) * mm, "mid": v(11.5, -24.52) * mm, "end": v(13.12, -25.15) * mm});
            skLineSegment(sketch, "E44.9.8", {"start": v(10.12, -23.46) * mm, "end": v(9.45, -21.84) * mm});
            skArc(sketch, "E44.9.9", {"start": v(9.45, -21.84) * mm, "mid": v(8.62, -20.99) * mm, "end": v(7.44, -20.94) * mm});
            skArc(sketch, "E44.10.0", {"start": v(19.05, -11.45) * mm, "mid": v(18.86, -12.62) * mm, "end": v(19.53, -13.6) * mm});
            skLineSegment(sketch, "E44.10.1", {"start": v(20.98, -14.58) * mm, "end": v(19.53, -13.6) * mm});
            skArc(sketch, "E44.10.2", {"start": v(20.98, -14.58) * mm, "mid": v(21.75, -16.14) * mm, "end": v(22.05, -17.85) * mm});
            skArc(sketch, "E44.10.3", {"start": v(21.96, -18.15) * mm, "mid": v(22.03, -18.01) * mm, "end": v(22.05, -17.85) * mm});
            skLineSegment(sketch, "E44.10.4", {"start": v(21.99, -18.11) * mm, "end": v(21.96, -18.15) * mm});
            skLineSegment(sketch, "E44.10.5", {"start": v(21.99, -18.11) * mm, "end": v(22.02, -18.08) * mm});
            skArc(sketch, "E44.10.6", {"start": v(21.75, -18.22) * mm, "mid": v(21.9, -18.17) * mm, "end": v(22.02, -18.08) * mm});
            skArc(sketch, "E44.10.7", {"start": v(18.33, -17.8) * mm, "mid": v(20, -18.25) * mm, "end": v(21.75, -18.22) * mm});
            skLineSegment(sketch, "E44.10.8", {"start": v(18.33, -17.8) * mm, "end": v(17.1, -16.56) * mm});
            skArc(sketch, "E44.10.9", {"start": v(17.1, -16.56) * mm, "mid": v(16, -16.1) * mm, "end": v(14.89, -16.5) * mm});
            skArc(sketch, "E44.11.0", {"start": v(21.98, -3.29) * mm, "mid": v(22.25, -4.44) * mm, "end": v(23.25, -5.1) * mm});
            skLineSegment(sketch, "E44.11.1", {"start": v(24.96, -5.44) * mm, "end": v(23.25, -5.1) * mm});
            skArc(sketch, "E44.11.2", {"start": v(24.96, -5.44) * mm, "mid": v(26.27, -6.59) * mm, "end": v(27.2, -8.06) * mm});
            skArc(sketch, "E44.11.3", {"start": v(27.23, -8.37) * mm, "mid": v(27.24, -8.21) * mm, "end": v(27.2, -8.06) * mm});
            skLineSegment(sketch, "E44.11.4", {"start": v(27.24, -8.32) * mm, "end": v(27.23, -8.37) * mm});
            skLineSegment(sketch, "E44.11.5", {"start": v(27.24, -8.32) * mm, "end": v(27.26, -8.27) * mm});
            skArc(sketch, "E44.11.6", {"start": v(27.06, -8.5) * mm, "mid": v(27.18, -8.4) * mm, "end": v(27.26, -8.27) * mm});
            skArc(sketch, "E44.11.7", {"start": v(23.74, -9.43) * mm, "mid": v(25.47, -9.2) * mm, "end": v(27.06, -8.5) * mm});
            skLineSegment(sketch, "E44.11.8", {"start": v(23.74, -9.43) * mm, "end": v(22.13, -8.76) * mm});
            skArc(sketch, "E44.11.9", {"start": v(22.13, -8.76) * mm, "mid": v(20.94, -8.74) * mm, "end": v(20.07, -9.55) * mm});
            skArc(sketch, "E44.12.0", {"start": v(21.57, 5.37) * mm, "mid": v(22.26, 4.4) * mm, "end": v(23.43, 4.19) * mm});
            skLineSegment(sketch, "E44.12.1", {"start": v(25.15, 4.53) * mm, "end": v(23.43, 4.19) * mm});
            skArc(sketch, "E44.12.2", {"start": v(25.15, 4.53) * mm, "mid": v(26.8, 3.96) * mm, "end": v(28.21, 2.96) * mm});
            skArc(sketch, "E44.12.3", {"start": v(28.36, 2.7) * mm, "mid": v(28.31, 2.84) * mm, "end": v(28.21, 2.96) * mm});
            skLineSegment(sketch, "E44.12.4", {"start": v(28.35, 2.74) * mm, "end": v(28.36, 2.7) * mm});
            skLineSegment(sketch, "E44.12.5", {"start": v(28.35, 2.74) * mm, "end": v(28.35, 2.8) * mm});
            skArc(sketch, "E44.12.6", {"start": v(28.26, 2.5) * mm, "mid": v(28.33, 2.64) * mm, "end": v(28.35, 2.8) * mm});
            skArc(sketch, "E44.12.7", {"start": v(25.55, 0.37) * mm, "mid": v(27.05, 1.24) * mm, "end": v(28.26, 2.5) * mm});
            skLineSegment(sketch, "E44.12.8", {"start": v(25.55, 0.37) * mm, "end": v(23.8, 0.38) * mm});
            skArc(sketch, "E44.12.9", {"start": v(23.8, 0.38) * mm, "mid": v(22.7, -0.06) * mm, "end": v(22.2, -1.14) * mm});
            skArc(sketch, "E44.13.0", {"start": v(17.87, 13.22) * mm, "mid": v(18.88, 12.6) * mm, "end": v(20.04, 12.83) * mm});
            skLineSegment(sketch, "E44.13.1", {"start": v(21.5, 13.8) * mm, "end": v(20.04, 12.83) * mm});
            skArc(sketch, "E44.13.2", {"start": v(21.5, 13.8) * mm, "mid": v(23.23, 13.92) * mm, "end": v(24.93, 13.54) * mm});
            skArc(sketch, "E44.13.3", {"start": v(25.17, 13.34) * mm, "mid": v(25.07, 13.46) * mm, "end": v(24.93, 13.54) * mm});
            skLineSegment(sketch, "E44.13.4", {"start": v(25.15, 13.38) * mm, "end": v(25.17, 13.34) * mm});
            skLineSegment(sketch, "E44.13.5", {"start": v(25.15, 13.38) * mm, "end": v(25.13, 13.43) * mm});
            skArc(sketch, "E44.13.6", {"start": v(25.15, 13.12) * mm, "mid": v(25.16, 13.28) * mm, "end": v(25.13, 13.43) * mm});
            skArc(sketch, "E44.13.7", {"start": v(23.46, 10.12) * mm, "mid": v(24.52, 11.5) * mm, "end": v(25.15, 13.12) * mm});
            skLineSegment(sketch, "E44.13.8", {"start": v(23.46, 10.12) * mm, "end": v(21.84, 9.45) * mm});
            skArc(sketch, "E44.13.9", {"start": v(21.84, 9.45) * mm, "mid": v(20.99, 8.62) * mm, "end": v(20.94, 7.44) * mm});
            skArc(sketch, "E44.14.0", {"start": v(11.45, 19.05) * mm, "mid": v(12.62, 18.86) * mm, "end": v(13.6, 19.53) * mm});
            skLineSegment(sketch, "E44.14.1", {"start": v(14.58, 20.98) * mm, "end": v(13.6, 19.53) * mm});
            skArc(sketch, "E44.14.2", {"start": v(14.58, 20.98) * mm, "mid": v(16.14, 21.75) * mm, "end": v(17.85, 22.05) * mm});
            skArc(sketch, "E44.14.3", {"start": v(18.15, 21.96) * mm, "mid": v(18.01, 22.03) * mm, "end": v(17.85, 22.05) * mm});
            skLineSegment(sketch, "E44.14.4", {"start": v(18.11, 21.99) * mm, "end": v(18.15, 21.96) * mm});
            skLineSegment(sketch, "E44.14.5", {"start": v(18.11, 21.99) * mm, "end": v(18.08, 22.02) * mm});
            skArc(sketch, "E44.14.6", {"start": v(18.22, 21.75) * mm, "mid": v(18.17, 21.9) * mm, "end": v(18.08, 22.02) * mm});
            skArc(sketch, "E44.14.7", {"start": v(17.8, 18.33) * mm, "mid": v(18.25, 20) * mm, "end": v(18.22, 21.75) * mm});
            skLineSegment(sketch, "E44.14.8", {"start": v(17.8, 18.33) * mm, "end": v(16.56, 17.1) * mm});
            skArc(sketch, "E44.14.9", {"start": v(16.56, 17.1) * mm, "mid": v(16.1, 16) * mm, "end": v(16.5, 14.89) * mm});
            skArc(sketch, "E44.15.0", {"start": v(3.29, 21.98) * mm, "mid": v(4.44, 22.25) * mm, "end": v(5.1, 23.25) * mm});
            skLineSegment(sketch, "E44.15.1", {"start": v(5.44, 24.96) * mm, "end": v(5.1, 23.25) * mm});
            skArc(sketch, "E44.15.2", {"start": v(5.44, 24.96) * mm, "mid": v(6.59, 26.27) * mm, "end": v(8.06, 27.2) * mm});
            skArc(sketch, "E44.15.3", {"start": v(8.37, 27.23) * mm, "mid": v(8.21, 27.24) * mm, "end": v(8.06, 27.2) * mm});
            skLineSegment(sketch, "E44.15.4", {"start": v(8.32, 27.24) * mm, "end": v(8.37, 27.23) * mm});
            skLineSegment(sketch, "E44.15.5", {"start": v(8.32, 27.24) * mm, "end": v(8.27, 27.26) * mm});
            skArc(sketch, "E44.15.6", {"start": v(8.5, 27.06) * mm, "mid": v(8.4, 27.18) * mm, "end": v(8.27, 27.26) * mm});
            skArc(sketch, "E44.15.7", {"start": v(9.43, 23.74) * mm, "mid": v(9.2, 25.47) * mm, "end": v(8.5, 27.06) * mm});
            skLineSegment(sketch, "E44.15.8", {"start": v(9.43, 23.74) * mm, "end": v(8.76, 22.13) * mm});
            skArc(sketch, "E44.15.9", {"start": v(8.76, 22.13) * mm, "mid": v(8.74, 20.94) * mm, "end": v(9.55, 20.07) * mm});
            skArc(sketch, "E45.trimOffspring", {"start": v(-13.22, 17.87) * mm, "mid": v(-14.07, 17.2) * mm, "end": v(-14.89, 16.5) * mm});
            skArc(sketch, "E46.trimOffspring", {"start": v(-19.05, 11.45) * mm, "mid": v(-19.58, 10.51) * mm, "end": v(-20.07, 9.55) * mm});
            skArc(sketch, "E47.trimOffspring", {"start": v(-21.98, 3.29) * mm, "mid": v(-22.11, 2.22) * mm, "end": v(-22.2, 1.14) * mm});
            skArc(sketch, "E48.trimOffspring", {"start": v(3.29, 21.98) * mm, "mid": v(2.22, 22.11) * mm, "end": v(1.14, 22.2) * mm});
            skArc(sketch, "E49.trimOffspring", {"start": v(11.45, 19.05) * mm, "mid": v(10.51, 19.58) * mm, "end": v(9.55, 20.07) * mm});
            skArc(sketch, "E50.trimOffspring", {"start": v(17.87, 13.22) * mm, "mid": v(17.2, 14.07) * mm, "end": v(16.5, 14.89) * mm});
            skArc(sketch, "E51.trimOffspring", {"start": v(21.57, 5.37) * mm, "mid": v(21.28, 6.41) * mm, "end": v(20.94, 7.44) * mm});
            skArc(sketch, "E52.trimOffspring", {"start": v(21.98, -3.29) * mm, "mid": v(22.11, -2.22) * mm, "end": v(22.2, -1.14) * mm});
            skArc(sketch, "E53.trimOffspring", {"start": v(19.05, -11.45) * mm, "mid": v(19.58, -10.51) * mm, "end": v(20.07, -9.55) * mm});
            skArc(sketch, "E54.trimOffspring", {"start": v(13.22, -17.87) * mm, "mid": v(14.07, -17.2) * mm, "end": v(14.89, -16.5) * mm});
            skArc(sketch, "E55.trimOffspring", {"start": v(5.37, -21.57) * mm, "mid": v(6.41, -21.28) * mm, "end": v(7.44, -20.94) * mm});
            skArc(sketch, "E56.trimOffspring", {"start": v(-3.29, -21.98) * mm, "mid": v(-2.22, -22.11) * mm, "end": v(-1.14, -22.2) * mm});
            skArc(sketch, "E57.trimOffspring", {"start": v(-11.45, -19.05) * mm, "mid": v(-10.51, -19.58) * mm, "end": v(-9.55, -20.07) * mm});
            skArc(sketch, "E58.trimOffspring", {"start": v(-17.87, -13.22) * mm, "mid": v(-17.2, -14.07) * mm, "end": v(-16.5, -14.89) * mm});
            skArc(sketch, "E59.trimOffspring", {"start": v(-21.57, -5.37) * mm, "mid": v(-21.28, -6.41) * mm, "end": v(-20.94, -7.44) * mm});
            skSolve(sketch);
        }
        {
            var Q0;
            Q0=makeQuery(id+"F0.imprint","IMPRINT",FACE,{"disambiguationData":[TD([[makeQuery(id+"F0.imprint","IMPRINT",EDGE,{"derivedFrom":sQuery(id+"F0.wireOp",EDGE,"E0")}),1.0]])]});
            var Q1;
            Q1=makeQuery(id+"F2.imprint","IMPRINT",FACE,{"disambiguationData":[TD([[makeQuery(id+"F2.imprint","IMPRINT",EDGE,{"derivedFrom":sQuery(id+"F2.wireOp",EDGE,"E30")}),1.0]])]});
            var Q2;
            Q2=sQuery(id+"F0.wireOp",VERTEX,"E6.MirrorCS.end");
            var Q3;
            Q3=sQuery(id+"F2.wireOp",VERTEX,"E44.1.2.end");
            loft(context, id + "F3", {"sheetProfilesArray" : [{ "sheetProfileEntities" : qUnion([Q0]) }, { "sheetProfileEntities" : qUnion([Q1]) }], "matchConnections" : true, "connections" : [{ "connectionEntities" : qUnion([Q2, Q3]), "connectionEdgeQueries" : qUnion([]), "connectionEdgeParameters" : [] }]});
        }
        {
            var Q0;
            Q0=makeQuery(id+"F3.opLoft","CAP_FACE",FACE,{"disambiguationData":[OSD([makeQuery(id+"F2.imprint","IMPRINT",FACE,{"disambiguationData":[TD([[makeQuery(id+"F2.imprint","IMPRINT",EDGE,{"derivedFrom":sQuery(id+"F2.wireOp",EDGE,"E30")}),1.0]])]})])],"isStart":true});
            var sketch = newSketch(context, id + "F4", { "sketchPlane" : qUnion([Q0])});
            skCircle(sketch, "E60", {"center": v(0, 0) * mm, "radius": 6.35 * mm});
            skSolve(sketch);
        }
        {
            var Q0;
            Q0 = qSketchRegion(id + "F4", true);
            extrude(context, id + "F5", {"entities" : qUnion([Q0]), "operationType" : NewBodyOperationType.REMOVE, "endBound" : BoundingType.THROUGH_ALL, "oppositeDirection" : true, "depth" : 25.4 * mm});
        }
    });
